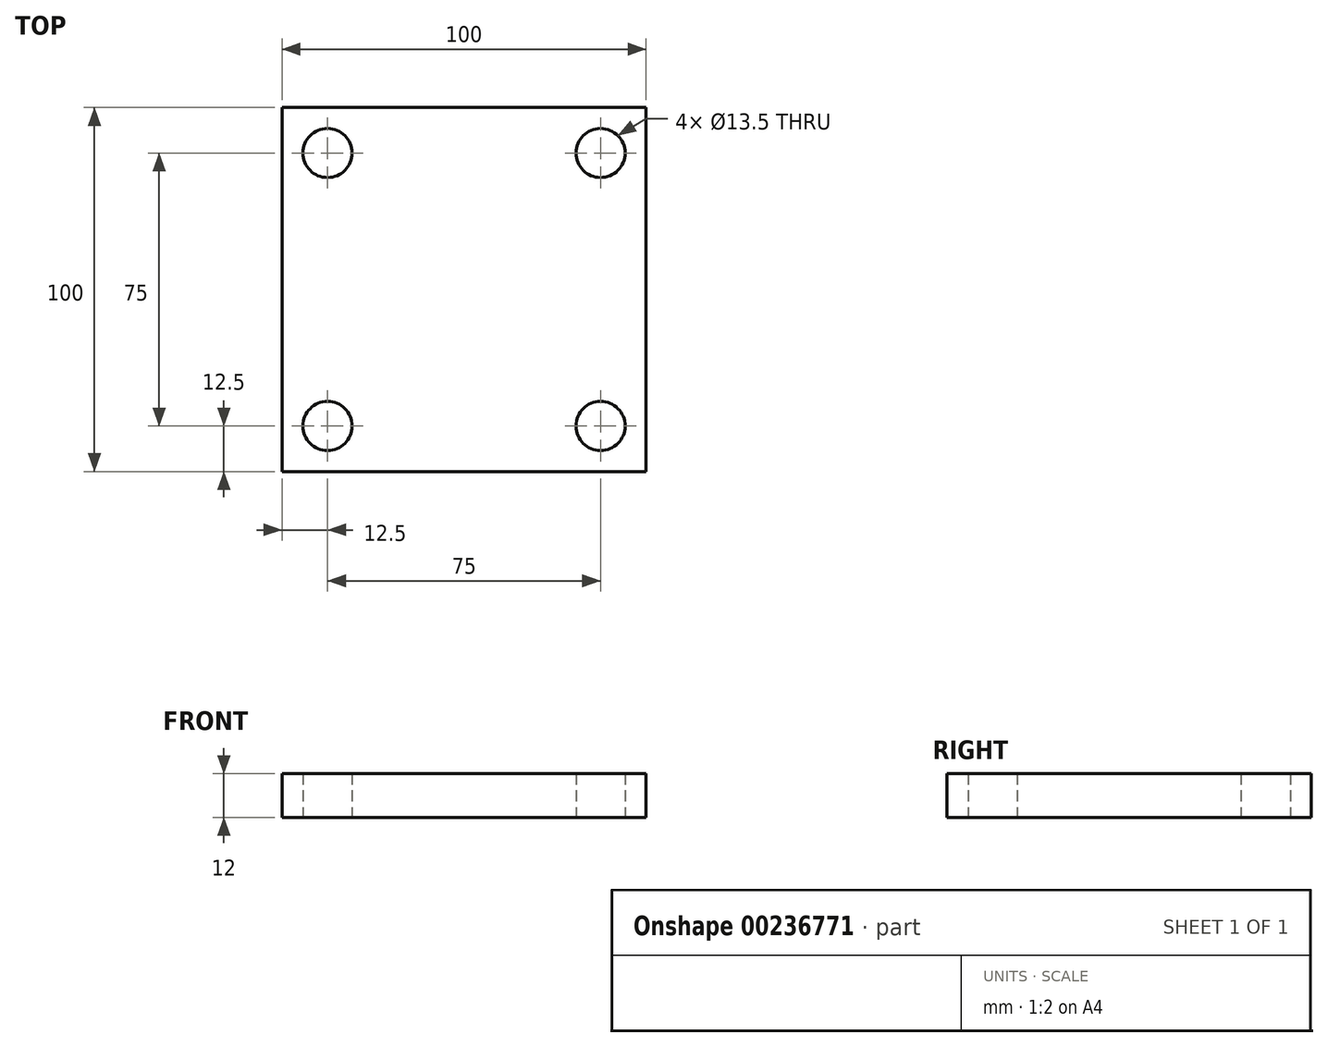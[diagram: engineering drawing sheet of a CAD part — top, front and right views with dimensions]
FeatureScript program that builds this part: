
annotation { "Feature Type Name" : "Feature", "Feature Type Description" : "" }
export const myFeature = defineFeature(function(context is Context, id is Id, definition is map)
    precondition{}
    {
        {
            var Q0;
            Q0=qCreatedBy(makeId("Top.planeOp"),FACE);
            var sketch = newSketch(context, id + "F0", { "sketchPlane" : qUnion([Q0])});
            skLineSegment(sketch, "E0.bottom", {"start": v(50, 50) * mm, "end": v(-50, 50) * mm});
            skLineSegment(sketch, "E0.top", {"start": v(50, -50) * mm, "end": v(-50, -50) * mm});
            skLineSegment(sketch, "E0.left", {"start": v(50, 50) * mm, "end": v(50, -50) * mm});
            skLineSegment(sketch, "E0.right", {"start": v(-50, 50) * mm, "end": v(-50, -50) * mm});
            skPoint(sketch, "E0.middle", {"position": v(0, 0) * mm});
            skSolve(sketch);
        }
        {
            var Q0;
            Q0 = qSketchRegion(id + "F0", true);
            extrude(context, id + "F1", {"entities" : qUnion([Q0]), "depth" : 12 * mm, "offsetDistance" : 25 * mm});
        }
        {
            var Q0;
            Q0=makeQuery(id+"F1.opExtrude","CAP_FACE",FACE,{"disambiguationData":[OSD([sQuery(id+"F0.wireOp",EDGE,"E0.bottom"),sQuery(id+"F0.wireOp",EDGE,"E0.top"),sQuery(id+"F0.wireOp",EDGE,"E0.left"),sQuery(id+"F0.wireOp",EDGE,"E0.right")])],"isStart":false});
            var sketch = newSketch(context, id + "F2", { "sketchPlane" : qUnion([Q0])});
            skPoint(sketch, "E1", {"position": v(-37.5, 37.5) * mm});
            skPoint(sketch, "E2", {"position": v(37.5, 37.5) * mm});
            skPoint(sketch, "E3", {"position": v(37.5, -37.5) * mm});
            skPoint(sketch, "E4", {"position": v(-37.5, -37.5) * mm});
            skSolve(sketch);
        }
        {
            var Q0;
            Q0=sQuery(id+"F2.wireOp",VERTEX,"E1");
            var Q1;
            Q1=sQuery(id+"F2.wireOp",VERTEX,"E2");
            var Q2;
            Q2=sQuery(id+"F2.wireOp",VERTEX,"E3");
            var Q3;
            Q3=sQuery(id+"F2.wireOp",VERTEX,"E4");
            var Q4;
            Q4=makeQuery(id+"F1.opExtrude","SWEPT_BODY",BODY,{"disambiguationData":[OSD([sQuery(id+"F0.wireOp",EDGE,"E0.bottom"),sQuery(id+"F0.wireOp",EDGE,"E0.top"),sQuery(id+"F0.wireOp",EDGE,"E0.left"),sQuery(id+"F0.wireOp",EDGE,"E0.right")])]});
            hole(context, id + "F3", {"style" : HoleStyle.SIMPLE, "endStyle" : HoleEndStyle.BLIND, "standardTappedOrClearance" : lookupTablePath({ "fit" : "Normal", "standard" : "ISO", "size" : "M12", "type" : "Clearance" }), "standardBlindInLast" : lookupTablePath({ "fit" : "Normal", "standard" : "ISO", "engagement" : "75%", "pitch" : "1.75 mm", "size" : "M12", "type" : "Clearance & tapped" }), "holeDiameter" : 13.5 * mm, "majorDiameter" : 5 * mm, "holeDepth" : 25 * mm, "isTappedThrough" : true, "tappedDepth" : 31.25 * mm, "tapClearance" : 3, "startFromSketch" : true, "locations" : qUnion([Q0, Q1, Q2, Q3]), "scope" : qUnion([Q4])});
        }
    });
